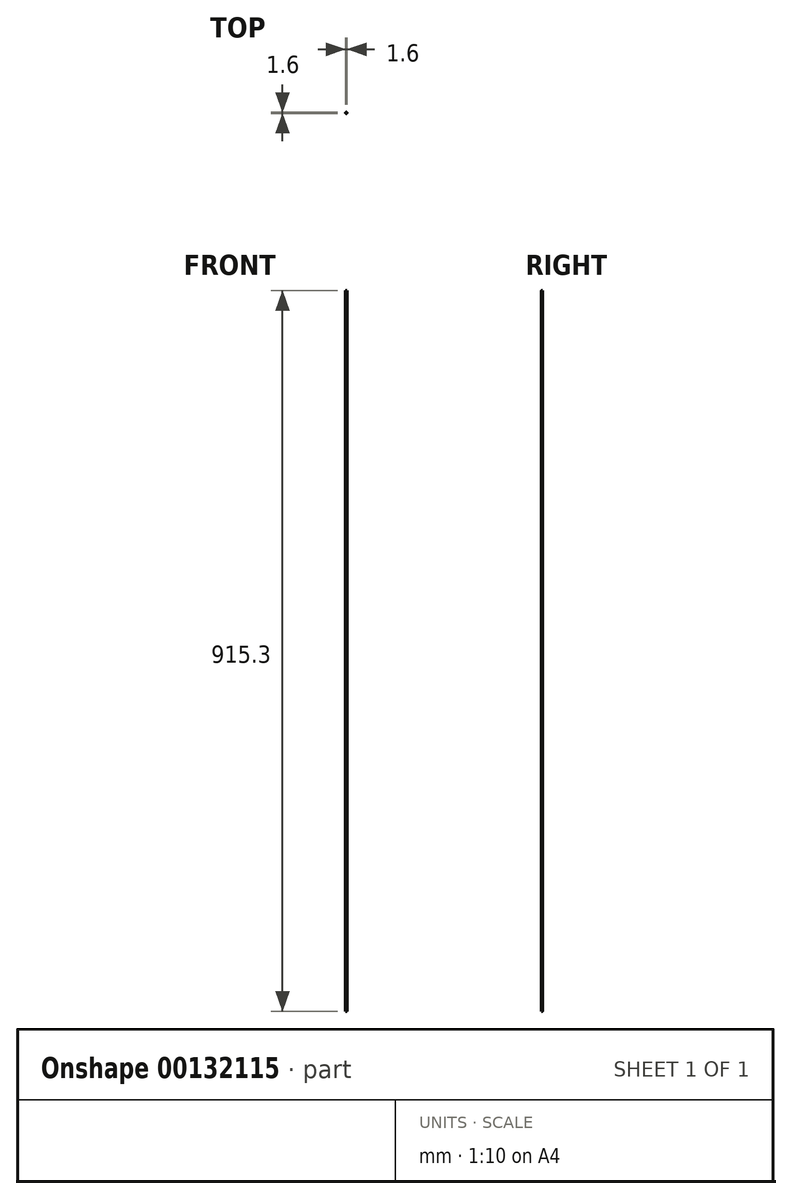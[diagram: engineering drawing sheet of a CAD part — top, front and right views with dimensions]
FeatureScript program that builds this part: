
annotation { "Feature Type Name" : "Feature", "Feature Type Description" : "" }
export const myFeature = defineFeature(function(context is Context, id is Id, definition is map)
    precondition{}
    {
        {
            var Q0;
            Q0=qCreatedBy(makeId("Top.planeOp"),FACE);
            var sketch = newSketch(context, id + "F0", { "sketchPlane" : qUnion([Q0])});
            skCircle(sketch, "E0", {"center": v(0, 0) * mm, "radius": 0.8 * mm});
            skSolve(sketch);
        }
        {
            var Q0;
            Q0 = qSketchRegion(id + "F0", true);
            extrude(context, id + "F1", {"entities" : qUnion([Q0]), "depth" : 915.3 * mm});
        }
    });
